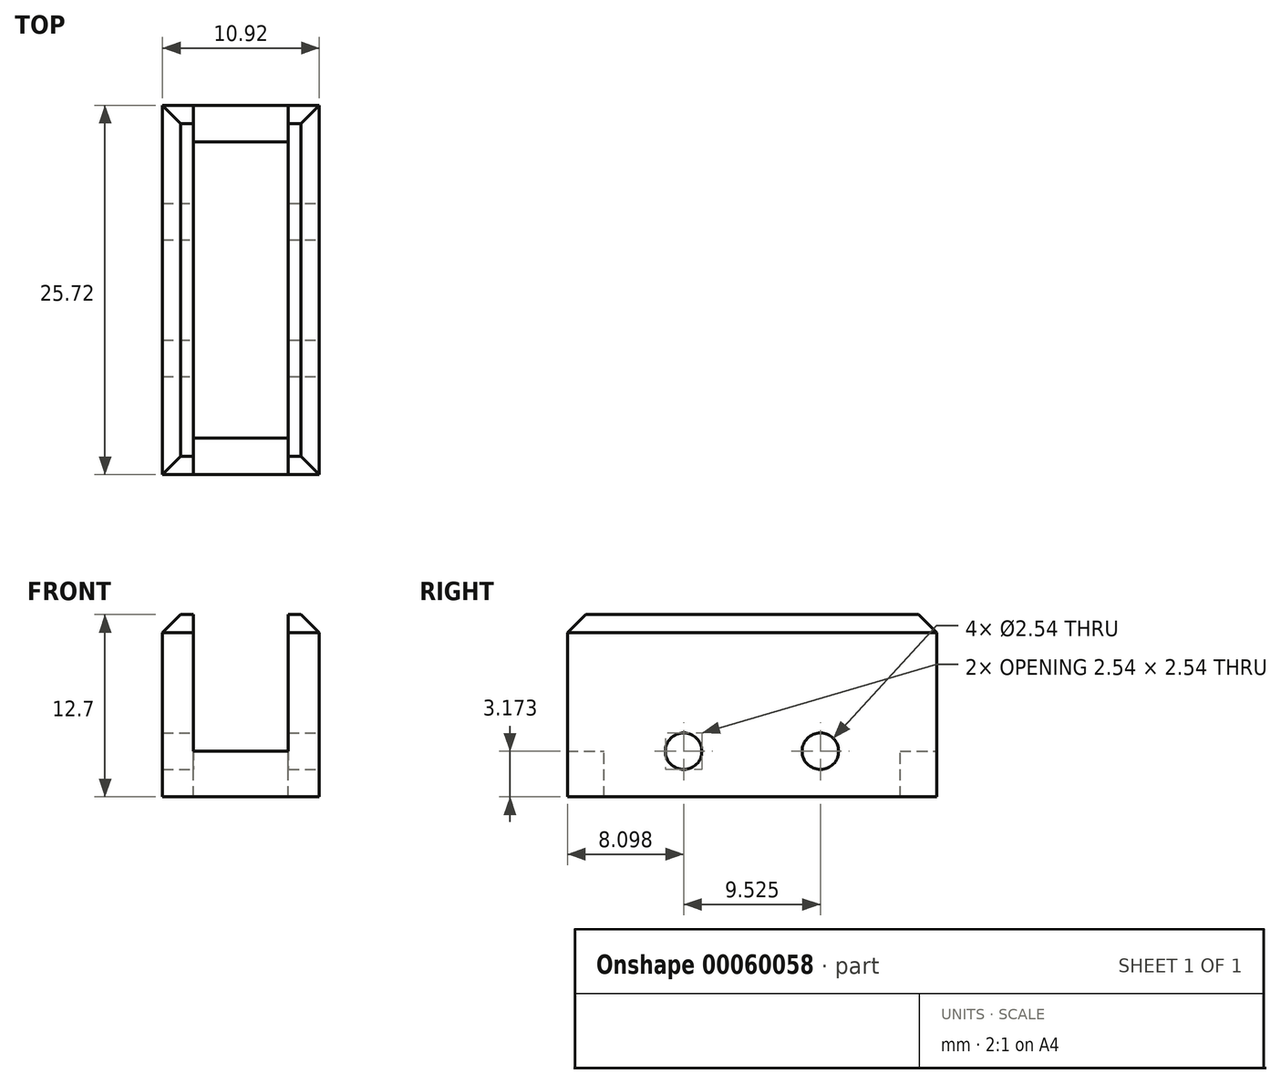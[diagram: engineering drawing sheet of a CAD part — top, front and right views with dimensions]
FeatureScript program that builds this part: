
annotation { "Feature Type Name" : "Feature", "Feature Type Description" : "" }
export const myFeature = defineFeature(function(context is Context, id is Id, definition is map)
    precondition{}
    {
        {
            var Q0;
            Q0=qCreatedBy(makeId("Top.planeOp"),FACE);
            var sketch = newSketch(context, id + "F0", { "sketchPlane" : qUnion([Q0])});
            skLineSegment(sketch, "E0.rect.bottom", {"start": v(5.46, 12.86) * mm, "end": v(-5.46, 12.86) * mm});
            skLineSegment(sketch, "E0.rect.top", {"start": v(5.46, -12.86) * mm, "end": v(-5.46, -12.86) * mm});
            skLineSegment(sketch, "E0.rect.left", {"start": v(5.46, 12.86) * mm, "end": v(5.46, -12.86) * mm});
            skLineSegment(sketch, "E0.rect.right", {"start": v(-5.46, 12.86) * mm, "end": v(-5.46, -12.86) * mm});
            skPoint(sketch, "E0.rect.middle", {"position": v(0, 0) * mm});
            skSolve(sketch);
        }
        {
            var Q0;
            Q0 = qSketchRegion(id + "F0", true);
            extrude(context, id + "F1", {"entities" : qUnion([Q0]), "depth" : 12.7 * mm});
        }
        {
            var Q0;
            Q0=makeQuery(id+"F1.opExtrude","CAP_FACE",FACE,{"disambiguationData":[OSD([sQuery(id+"F0.wireOp",EDGE,"E0.rect.bottom"),sQuery(id+"F0.wireOp",EDGE,"E0.rect.top"),sQuery(id+"F0.wireOp",EDGE,"E0.rect.left"),sQuery(id+"F0.wireOp",EDGE,"E0.rect.right")])],"isStart":false});
            var sketch = newSketch(context, id + "F2", { "sketchPlane" : qUnion([Q0])});
            skLineSegment(sketch, "E1.rect.bottom", {"start": v(-3.3, 10.32) * mm, "end": v(3.3, 10.32) * mm});
            skLineSegment(sketch, "E1.rect.top", {"start": v(-3.3, -10.32) * mm, "end": v(3.3, -10.32) * mm});
            skLineSegment(sketch, "E1.rect.left", {"start": v(-3.3, 10.32) * mm, "end": v(-3.3, -10.32) * mm});
            skLineSegment(sketch, "E1.rect.right", {"start": v(3.3, 10.32) * mm, "end": v(3.3, -10.32) * mm});
            skPoint(sketch, "E1.rect.middle", {"position": v(0, 0) * mm});
            skSolve(sketch);
        }
        {
            var Q0;
            Q0 = qSketchRegion(id + "F2", true);
            extrude(context, id + "F3", {"entities" : qUnion([Q0]), "operationType" : NewBodyOperationType.REMOVE, "oppositeDirection" : true, "depth" : 25.4 * mm});
        }
        {
            var Q0;
            Q0=makeQuery(id+"F1.opExtrude","SWEPT_FACE",FACE,{"disambiguationData":[OSD([sQuery(id+"F0.wireOp",EDGE,"E0.rect.bottom")])]});
            var sketch = newSketch(context, id + "F4", { "sketchPlane" : qUnion([Q0])});
            skLineSegment(sketch, "E2", {"start": v(0, 12.7) * mm, "end": v(0, 7.94) * mm});
            skPoint(sketch, "E2.endSnap0", {"position": v(0, 12.7) * mm});
            skLineSegment(sketch, "E3.rect.bottom", {"start": v(-3.3, 12.7) * mm, "end": v(3.3, 12.7) * mm});
            skLineSegment(sketch, "E3.rect.top", {"start": v(-3.3, 3.18) * mm, "end": v(3.3, 3.18) * mm});
            skLineSegment(sketch, "E3.rect.left", {"start": v(-3.3, 12.7) * mm, "end": v(-3.3, 3.18) * mm});
            skLineSegment(sketch, "E3.rect.right", {"start": v(3.3, 12.7) * mm, "end": v(3.3, 3.18) * mm});
            skPoint(sketch, "E3.rect.middle", {"position": v(0, 7.94) * mm});
            skSolve(sketch);
        }
        {
            var Q0;
            Q0 = qSketchRegion(id + "F4", true);
            extrude(context, id + "F5", {"entities" : qUnion([Q0]), "operationType" : NewBodyOperationType.REMOVE, "oppositeDirection" : true, "depth" : 32.18 * mm});
        }
        {
            var Q0;
            Q0=makeQuery(id+"F1.opExtrude","SWEPT_FACE",FACE,{"disambiguationData":[OSD([sQuery(id+"F0.wireOp",EDGE,"E0.rect.left")])]});
            var sketch = newSketch(context, id + "F6", { "sketchPlane" : qUnion([Q0])});
            skLineSegment(sketch, "E4", {"start": v(0, 0) * mm, "end": v(0, 3.17) * mm});
            skPoint(sketch, "E4.endSnap0", {"position": v(0, 0) * mm});
            skLineSegment(sketch, "E5", {"start": v(0, 3.17) * mm, "end": v(-4.76, 3.17) * mm});
            skCircle(sketch, "E6", {"center": v(-4.76, 3.17) * mm, "radius": 1.27 * mm});
            skCircle(sketch, "E7.MirrorC", {"center": v(4.76, 3.17) * mm, "radius": 1.27 * mm});
            skSolve(sketch);
        }
        {
            var Q0;
            Q0 = qSketchRegion(id + "F6", true);
            extrude(context, id + "F7", {"entities" : qUnion([Q0]), "operationType" : NewBodyOperationType.REMOVE, "oppositeDirection" : true, "depth" : 25.4 * mm});
        }
        {
            var Q0;
            Q0=makeQuery(id+"F1.opExtrude","CAP_EDGE",EDGE,{"disambiguationData":[OSD([sQuery(id+"F0.wireOp",EDGE,"E0.rect.right")])],"isStart":false});
            var Q1;
            Q1=makeQuery(id+"F1.opExtrude","CAP_EDGE",EDGE,{"disambiguationData":[OSD([sQuery(id+"F0.wireOp",EDGE,"E0.rect.left")])],"isStart":false});
            var Q2;
            {var subQ0=sQuery(id+"F0.wireOp",EDGE,"E0.rect.right");var subQ1=sQuery(id+"F0.wireOp",EDGE,"E0.rect.bottom");Q2=makeQuery(id+"F5.boolean.opBoolean","SPLIT",EDGE,{"disambiguationData":[TD([makeQuery(id+"F1.opExtrude","SWEPT_FACE",FACE,{"disambiguationData":[OSD([subQ0])]})])],"derivedFrom":makeQuery(id+"F1.opExtrude","CAP_EDGE",EDGE,{"disambiguationData":[OSD([subQ1])],"isStart":false})});}
            var Q3;
            {var subQ0=sQuery(id+"F0.wireOp",EDGE,"E0.rect.left");var subQ1=sQuery(id+"F0.wireOp",EDGE,"E0.rect.bottom");Q3=makeQuery(id+"F5.boolean.opBoolean","SPLIT",EDGE,{"disambiguationData":[TD([makeQuery(id+"F1.opExtrude","SWEPT_FACE",FACE,{"disambiguationData":[OSD([subQ0])]})])],"derivedFrom":makeQuery(id+"F1.opExtrude","CAP_EDGE",EDGE,{"disambiguationData":[OSD([subQ1])],"isStart":false})});}
            var Q4;
            {var subQ0=sQuery(id+"F0.wireOp",EDGE,"E0.rect.left");var subQ1=sQuery(id+"F0.wireOp",EDGE,"E0.rect.top");Q4=makeQuery(id+"F5.boolean.opBoolean","SPLIT",EDGE,{"disambiguationData":[TD([makeQuery(id+"F1.opExtrude","SWEPT_FACE",FACE,{"disambiguationData":[OSD([subQ0])]})])],"derivedFrom":makeQuery(id+"F1.opExtrude","CAP_EDGE",EDGE,{"disambiguationData":[OSD([subQ1])],"isStart":false})});}
            var Q5;
            {var subQ0=sQuery(id+"F0.wireOp",EDGE,"E0.rect.top");var subQ1=sQuery(id+"F0.wireOp",EDGE,"E0.rect.right");Q5=makeQuery(id+"F5.boolean.opBoolean","SPLIT",EDGE,{"disambiguationData":[TD([makeQuery(id+"F1.opExtrude","SWEPT_FACE",FACE,{"disambiguationData":[OSD([subQ1])]})])],"derivedFrom":makeQuery(id+"F1.opExtrude","CAP_EDGE",EDGE,{"disambiguationData":[OSD([subQ0])],"isStart":false})});}
            chamfer(context, id + "F8", {"entities" : qUnion([Q0, Q1, Q2, Q3, Q4, Q5]), "width" : 1.27 * mm, "tangentPropagation" : true});
        }
    });
